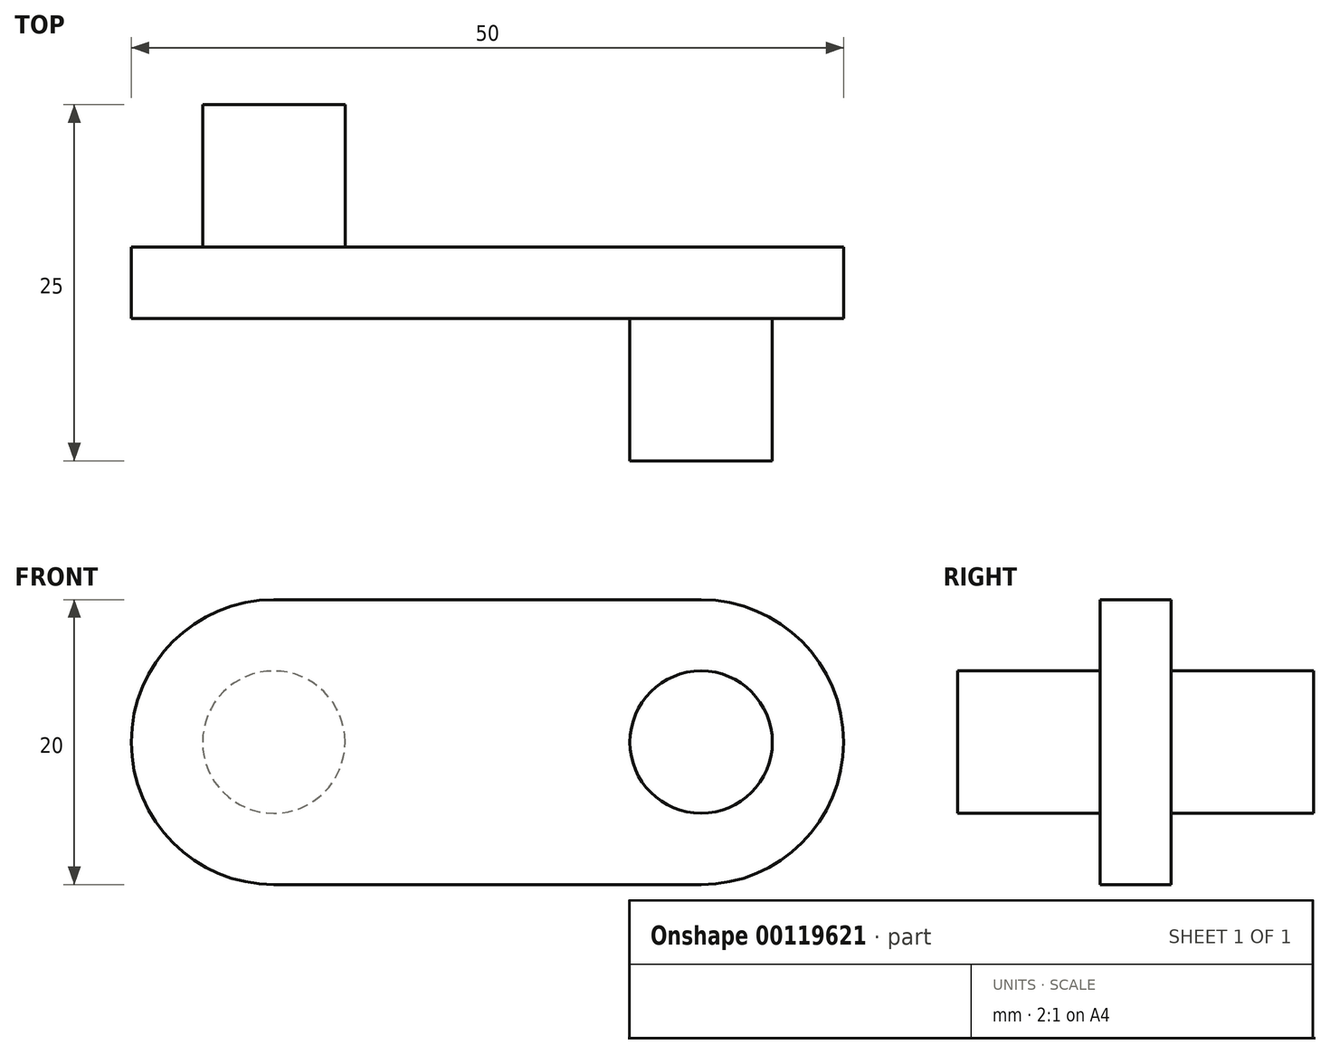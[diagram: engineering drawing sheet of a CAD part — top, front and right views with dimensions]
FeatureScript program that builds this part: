
annotation { "Feature Type Name" : "Feature", "Feature Type Description" : "" }
export const myFeature = defineFeature(function(context is Context, id is Id, definition is map)
    precondition{}
    {
        {
            var Q0;
            Q0=qCreatedBy(makeId("Front.planeOp"),FACE);
            var sketch = newSketch(context, id + "F0", { "sketchPlane" : qUnion([Q0])});
            skLineSegment(sketch, "E0.bottom", {"start": v(0, 0) * mm, "end": v(30, 0) * mm});
            skLineSegment(sketch, "E0.top", {"start": v(0, 20) * mm, "end": v(30, 20) * mm});
            skArc(sketch, "E1", {"start": v(0, 20) * mm, "mid": v(-10, 10) * mm, "end": v(0, 0) * mm});
            skArc(sketch, "E2", {"start": v(30, 0) * mm, "mid": v(40, 10) * mm, "end": v(30, 20) * mm});
            skSolve(sketch);
        }
        {
            var Q0;
            Q0 = qSketchRegion(id + "F0", true);
            extrude(context, id + "F1", {"entities" : qUnion([Q0]), "oppositeDirection" : true, "depth" : 5 * mm});
        }
        {
            var Q0;
            Q0=makeQuery(id+"F1.opExtrude","CAP_FACE",FACE,{"disambiguationData":[OSD([sQuery(id+"F0.wireOp",EDGE,"E0.bottom"),sQuery(id+"F0.wireOp",EDGE,"E0.top"),sQuery(id+"F0.wireOp",EDGE,"E1"),sQuery(id+"F0.wireOp",EDGE,"E2")])],"isStart":true});
            var sketch = newSketch(context, id + "F2", { "sketchPlane" : qUnion([Q0])});
            skCircle(sketch, "E3", {"center": v(30, 10) * mm, "radius": 5 * mm});
            skSolve(sketch);
        }
        {
            var Q0;
            Q0 = qSketchRegion(id + "F2", true);
            extrude(context, id + "F3", {"entities" : qUnion([Q0]), "operationType" : NewBodyOperationType.ADD, "depth" : 10 * mm});
        }
        {
            var Q0;
            Q0=makeQuery(id+"F1.opExtrude","CAP_FACE",FACE,{"disambiguationData":[OSD([sQuery(id+"F0.wireOp",EDGE,"E0.bottom"),sQuery(id+"F0.wireOp",EDGE,"E0.top"),sQuery(id+"F0.wireOp",EDGE,"E1"),sQuery(id+"F0.wireOp",EDGE,"E2")])],"isStart":false});
            var sketch = newSketch(context, id + "F4", { "sketchPlane" : qUnion([Q0])});
            skCircle(sketch, "E4", {"center": v(0, 10) * mm, "radius": 5 * mm});
            skSolve(sketch);
        }
        {
            var Q0;
            Q0 = qSketchRegion(id + "F4", true);
            extrude(context, id + "F5", {"entities" : qUnion([Q0]), "operationType" : NewBodyOperationType.ADD, "depth" : 10 * mm});
        }
    });
